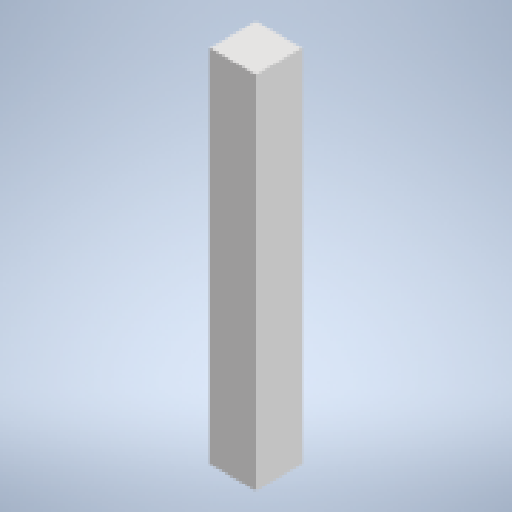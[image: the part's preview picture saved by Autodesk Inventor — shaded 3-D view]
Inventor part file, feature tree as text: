
AUTODESK INVENTOR PART (.ipt)
format: ipt  version: 2024 (Build 280153000, 153)  size: 133,120 bytes
history: native  units: mm
features: extrude x1, sketch x1
ambient origin geometry x8: Origin, YZ Plane, XZ Plane, XY Plane, X Axis, Y Axis, Z Axis, Center Point
bodies: Solid1 (feature_tree)
feature tree (2):
  extrude  "Extrusion1"  Depth=45.0mm
  sketch  "Sketch1"  dims[d0=45.0mm d1=45.0mm d2=350.0mm d3=0.0mm]
